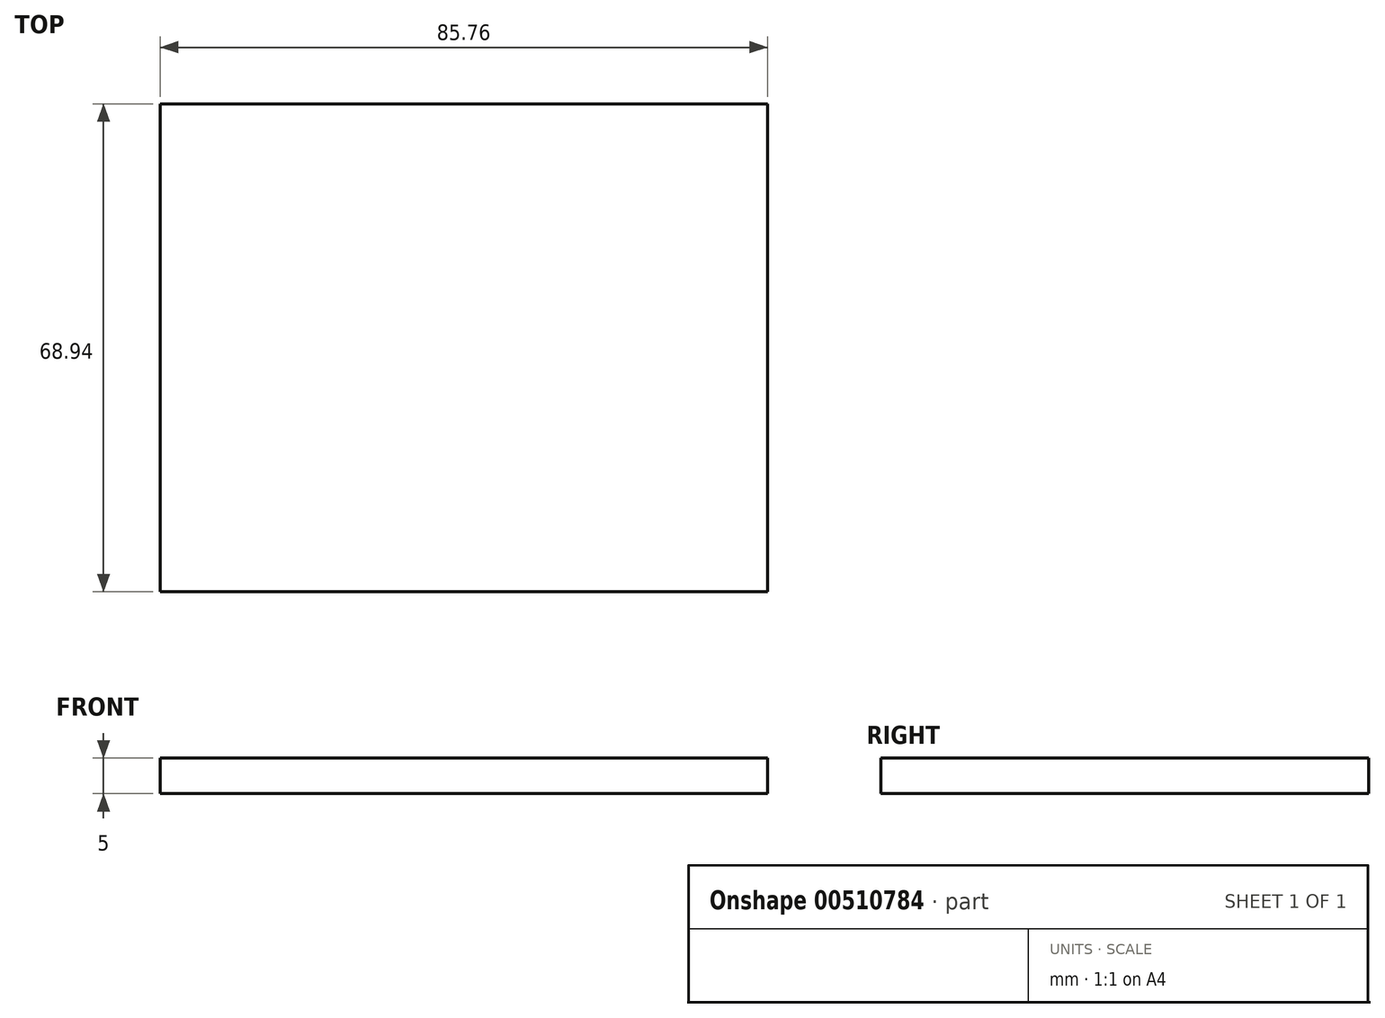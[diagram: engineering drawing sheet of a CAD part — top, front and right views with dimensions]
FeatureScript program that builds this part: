
annotation { "Feature Type Name" : "Feature", "Feature Type Description" : "" }
export const myFeature = defineFeature(function(context is Context, id is Id, definition is map)
    precondition{}
    {
        {
            var Q0;
            Q0=qCreatedBy(makeId("Top.planeOp"),FACE);
            var sketch = newSketch(context, id + "F0", { "sketchPlane" : qUnion([Q0])});
            skLineSegment(sketch, "E0.bottom", {"start": v(-40.4, 40.4) * mm, "end": v(45.36, 40.4) * mm});
            skLineSegment(sketch, "E0.top", {"start": v(-40.4, -28.53) * mm, "end": v(45.36, -28.53) * mm});
            skLineSegment(sketch, "E0.left", {"start": v(-40.4, 40.4) * mm, "end": v(-40.4, -28.53) * mm});
            skLineSegment(sketch, "E0.right", {"start": v(45.36, 40.4) * mm, "end": v(45.36, -28.53) * mm});
            skSolve(sketch);
        }
        {
            var Q0;
            Q0=makeQuery(id+"F0.imprint","IMPRINT",FACE,{"disambiguationData":[TD([[makeQuery(id+"F0.imprint","IMPRINT",EDGE,{"derivedFrom":sQuery(id+"F0.wireOp",EDGE,"E0.bottom")}),-1.0]])]});
            extrude(context, id + "F1", {"entities" : qUnion([Q0]), "depth" : 5 * mm});
        }
    });
